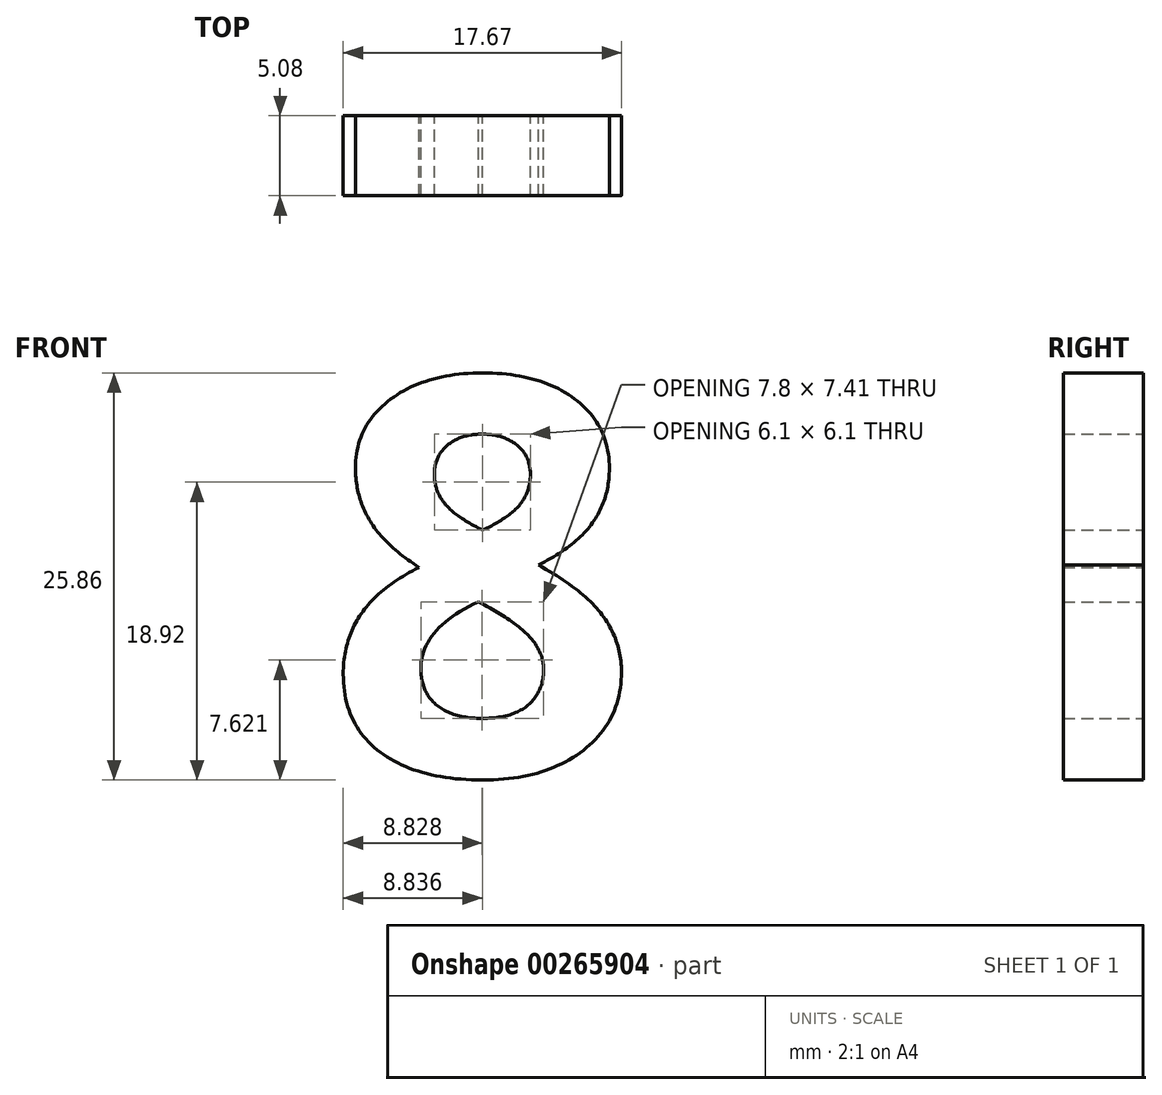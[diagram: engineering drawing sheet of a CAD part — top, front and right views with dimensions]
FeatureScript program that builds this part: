
annotation { "Feature Type Name" : "Feature", "Feature Type Description" : "" }
export const myFeature = defineFeature(function(context is Context, id is Id, definition is map)
    precondition{}
    {
        {
            var Q0;
            Q0=qCreatedBy(makeId("Front.planeOp"),FACE);
            var sketch = newSketch(context, id + "F0", { "sketchPlane" : qUnion([Q0])});
            skText(sketch, "E0", { "text": "8", "fontName": "OpenSans-Bold.ttf"});
            const initialGuessF0  = {"E0": [-0.06977, 0.00967, 1, 0, 0.0254]};
            skSetInitialGuess(sketch, initialGuessF0);
            skSolve(sketch);
        }
        {
            var Q0;
            Q0 = qSketchRegion(id + "F0", true);
            extrude(context, id + "F1", {"entities" : qUnion([Q0]), "depth" : 5.08 * mm});
        }
    });
